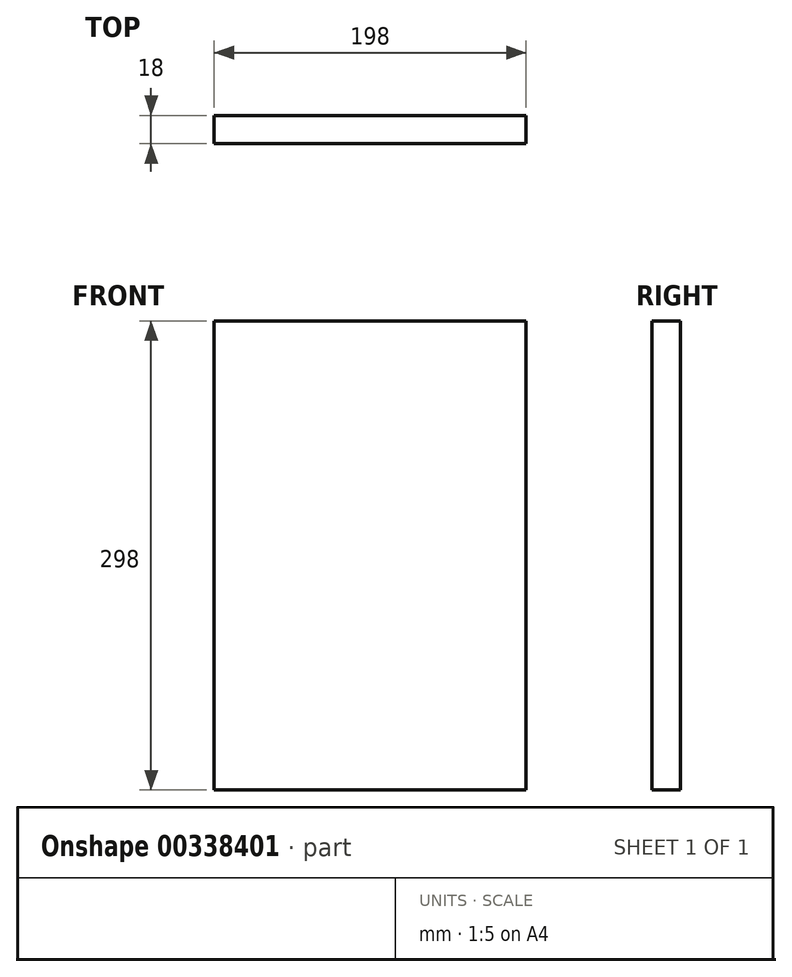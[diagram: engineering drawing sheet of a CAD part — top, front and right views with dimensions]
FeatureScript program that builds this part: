
annotation { "Feature Type Name" : "Feature", "Feature Type Description" : "" }
export const myFeature = defineFeature(function(context is Context, id is Id, definition is map)
    precondition{}
    {
        {
            var Q0;
            Q0=qCreatedBy(makeId("Front.planeOp"),FACE);
            var sketch = newSketch(context, id + "F0", { "sketchPlane" : qUnion([Q0])});
            skLineSegment(sketch, "E0.bottom", {"start": v(-99, 149) * mm, "end": v(99, 149) * mm});
            skLineSegment(sketch, "E0.top", {"start": v(-99, -149) * mm, "end": v(99, -149) * mm});
            skLineSegment(sketch, "E0.left", {"start": v(-99, 149) * mm, "end": v(-99, -149) * mm});
            skLineSegment(sketch, "E0.right", {"start": v(99, 149) * mm, "end": v(99, -149) * mm});
            skPoint(sketch, "E0.middle", {"position": v(0, 0) * mm});
            skSolve(sketch);
        }
        {
            var Q0;
            Q0=makeQuery(id+"F0.imprint","IMPRINT",FACE,{"disambiguationData":[TD([[makeQuery(id+"F0.imprint","IMPRINT",EDGE,{"derivedFrom":sQuery(id+"F0.wireOp",EDGE,"NIlTpRy1-X7Tk-jqVd-Orj9-Iw1hOTnxqfvd.right")}),-1.0]])]});
            var Q1;
            Q1=makeQuery(id+"F0.imprint","IMPRINT",FACE,{"disambiguationData":[TD([[makeQuery(id+"F0.imprint","IMPRINT",EDGE,{"derivedFrom":sQuery(id+"F0.wireOp",EDGE,"NIlTpRy1-X7Tk-jqVd-Orj9-Iw1hOTnxqfvd.bottom")}),1.0]])]});
            var Q2;
            Q2=makeQuery(id+"F0.imprint","IMPRINT",FACE,{"disambiguationData":[TD([[makeQuery(id+"F0.imprint","IMPRINT",EDGE,{"derivedFrom":sQuery(id+"F0.wireOp",EDGE,"NIlTpRy1-X7Tk-jqVd-Orj9-Iw1hOTnxqfvd.left")}),1.0]])]});
            var Q3;
            Q3=makeQuery(id+"F0.imprint","IMPRINT",FACE,{"disambiguationData":[TD([[makeQuery(id+"F0.imprint","IMPRINT",EDGE,{"derivedFrom":sQuery(id+"F0.wireOp",EDGE,"E0.bottom")}),-1.0]])]});
            extrude(context, id + "F1", {"entities" : qUnion([Q0, Q1, Q2, Q3]), "depth" : 18 * mm});
        }
    });
